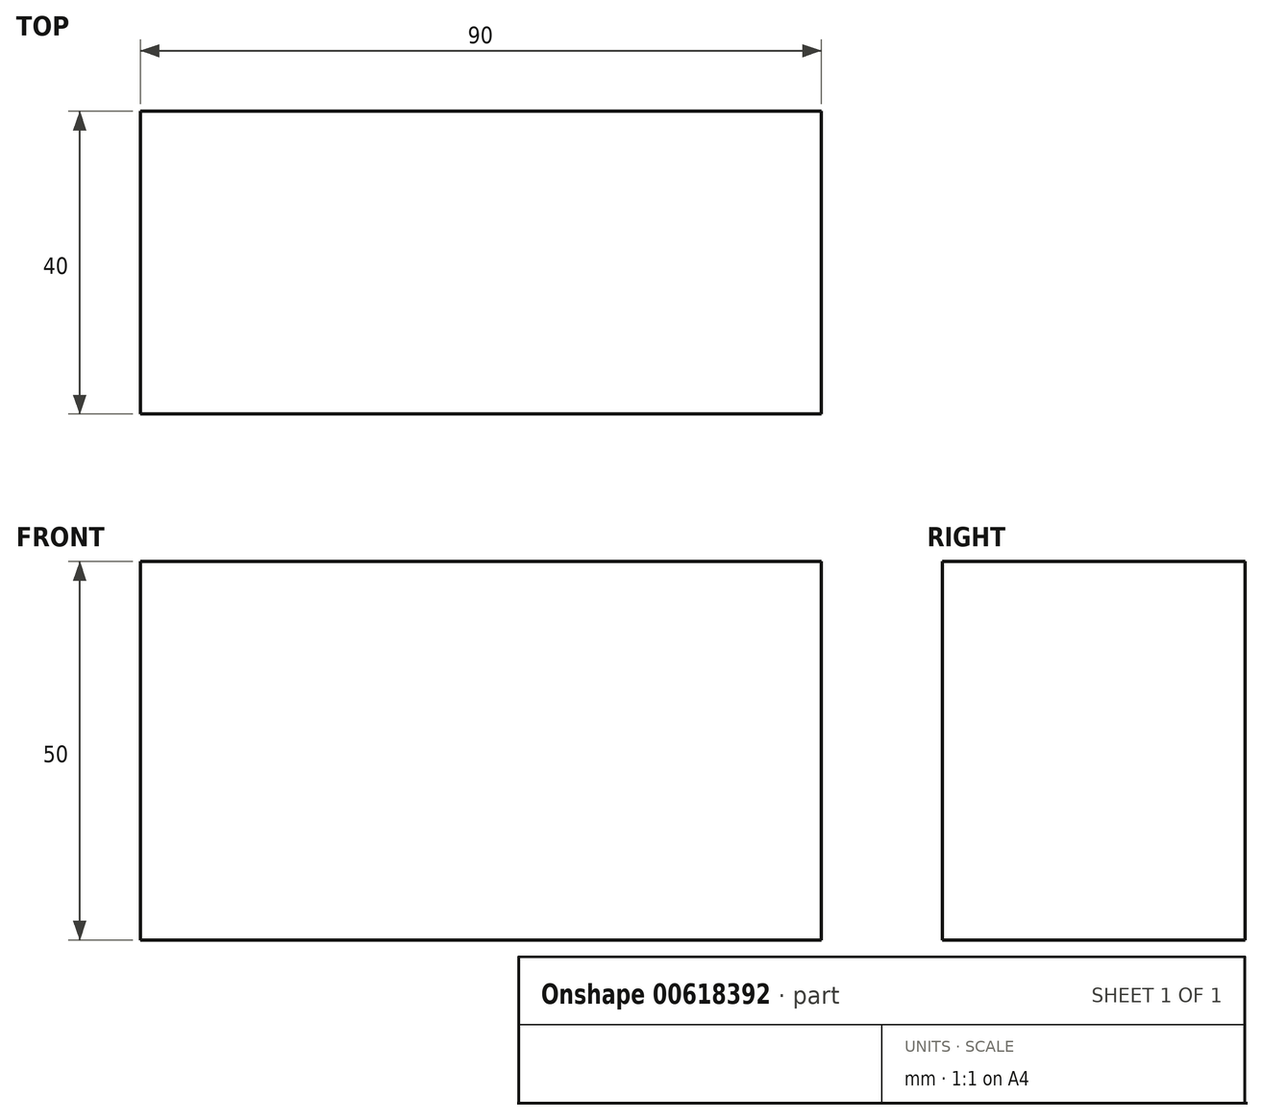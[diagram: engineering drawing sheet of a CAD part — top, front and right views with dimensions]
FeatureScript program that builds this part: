
annotation { "Feature Type Name" : "Feature", "Feature Type Description" : "" }
export const myFeature = defineFeature(function(context is Context, id is Id, definition is map)
    precondition{}
    {
        {
            var Q0;
            Q0=qCreatedBy(makeId("Top.planeOp"),FACE);
            var sketch = newSketch(context, id + "F0", { "sketchPlane" : qUnion([Q0])});
            skLineSegment(sketch, "E0.bottom", {"start": v(0, 0) * mm, "end": v(90, 0) * mm});
            skLineSegment(sketch, "E0.top", {"start": v(0, 40) * mm, "end": v(90, 40) * mm});
            skLineSegment(sketch, "E0.left", {"start": v(0, 0) * mm, "end": v(0, 40) * mm});
            skLineSegment(sketch, "E0.right", {"start": v(90, 0) * mm, "end": v(90, 40) * mm});
            skSolve(sketch);
        }
        {
            var Q0;
            Q0=makeQuery(id+"F0.imprint","IMPRINT",FACE,{"disambiguationData":[TD([[makeQuery(id+"F0.imprint","IMPRINT",EDGE,{"derivedFrom":sQuery(id+"F0.wireOp",EDGE,"E0.bottom")}),1.0]])]});
            extrude(context, id + "F1", {"entities" : qUnion([Q0]), "depth" : 50 * mm, "offsetDistance" : 25 * mm});
        }
    });
